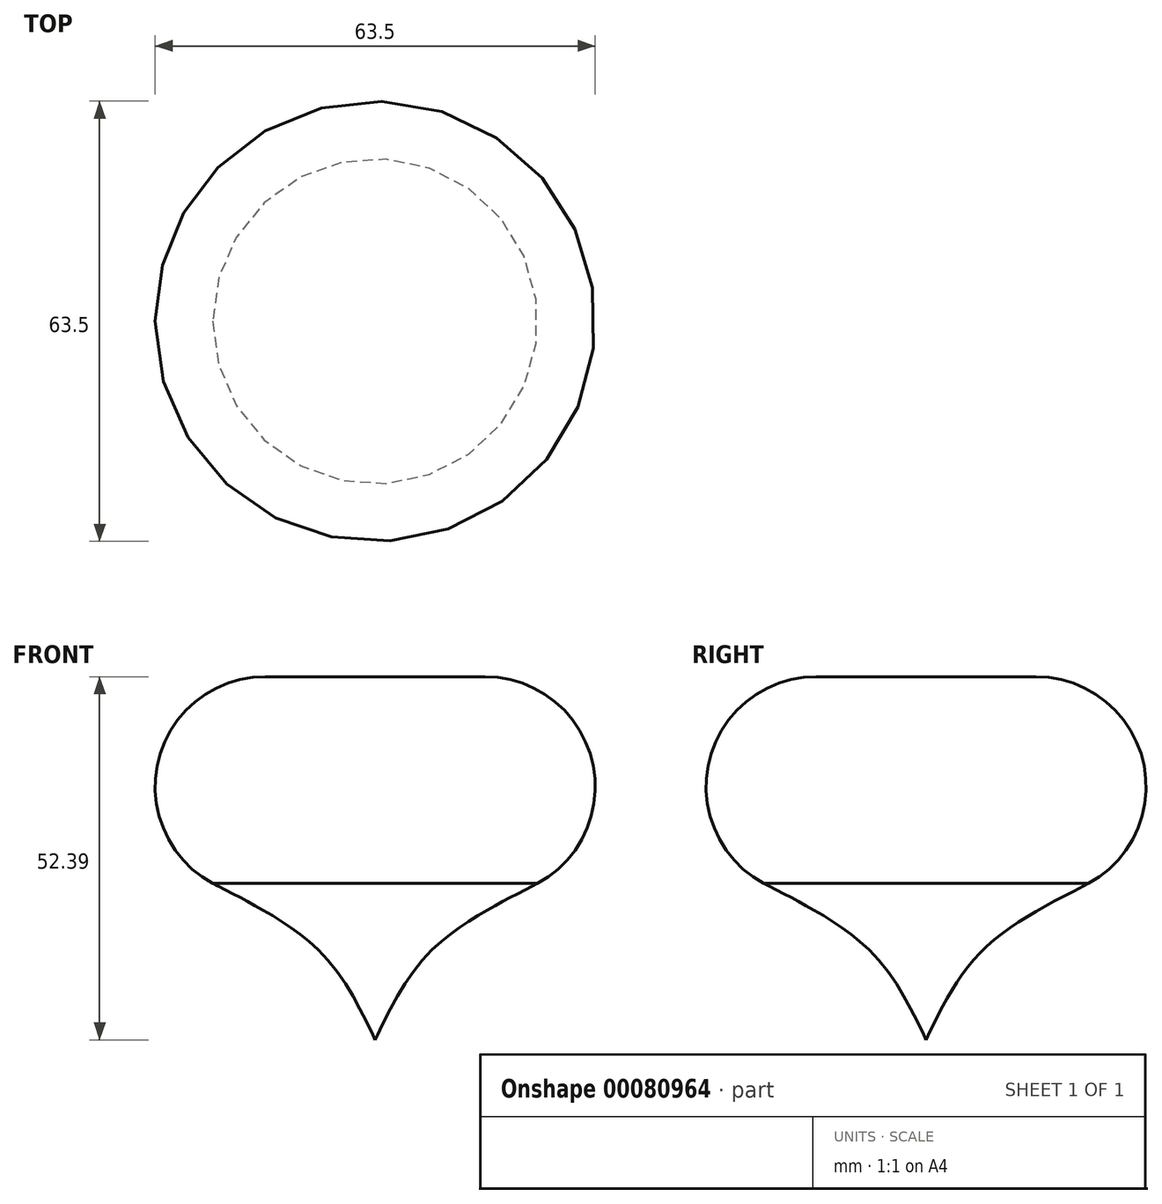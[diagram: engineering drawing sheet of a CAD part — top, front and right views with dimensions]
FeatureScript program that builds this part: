
annotation { "Feature Type Name" : "Feature", "Feature Type Description" : "" }
export const myFeature = defineFeature(function(context is Context, id is Id, definition is map)
    precondition{}
    {
        {
            var Q0;
            Q0=qCreatedBy(makeId("Right.planeOp"),FACE);
            var sketch = newSketch(context, id + "F0", { "sketchPlane" : qUnion([Q0])});
            skLineSegment(sketch, "E0", {"start": v(15.88, 31.75) * mm, "end": v(15.88, 47.62) * mm});
            skCircle(sketch, "E1", {"center": v(15.88, 47.62) * mm, "radius": 15.88 * mm});
            skLineSegment(sketch, "E2", {"start": v(0, 63.5) * mm, "end": v(15.87, 63.5) * mm});
            skFitSpline(sketch, "E3", {"points": [v(0, 11.11) * mm, v(7.94, 23.81) * mm, v(23.43, 33.66) * mm], "startDerivative": vector(13.7, 28.66) * mm, "endDerivative": vector(32.82, 16.67) * mm});
            skLineSegment(sketch, "E4", {"start": v(0, 11.11) * mm, "end": v(0, 63.5) * mm});
            skSolve(sketch);
        }
        {
            var Q0;
            {var subQ0=sQuery(id+"F0.wireOp",EDGE,"E2");Q0=makeQuery(id+"F0.imprint","IMPRINT",FACE,{"disambiguationData":[TD([[makeQuery(id+"F0.imprint","IMPRINT",EDGE,{"derivedFrom":subQ0}),-1.0]])]});}
            var Q1;
            {var subQ0=sQuery(id+"F0.wireOp",EDGE,"E1");var subQ4=makeQuery(id+"F0.imprint","IMPRINT",VERTEX,{"derivedFrom":subQ0});Q1=makeQuery(id+"F0.imprint","IMPRINT",FACE,{"disambiguationData":[TD([[makeQuery(id+"F0.imprint","IMPRINT",EDGE,{"disambiguationData":[TD([[subQ4,1.0]])],"derivedFrom":subQ0}),1.0]])]});}
            var Q2;
            {var subQ0=sQuery(id+"F0.wireOp",EDGE,"E1");var subQ1=makeQuery(id+"F0.imprint","IMPRINT",VERTEX,{"derivedFrom":subQ0});Q2=makeQuery(id+"F0.imprint","IMPRINT",FACE,{"disambiguationData":[TD([[makeQuery(id+"F0.imprint","IMPRINT",EDGE,{"disambiguationData":[TD([[subQ1,1.0]])],"derivedFrom":subQ0}),-1.0]])]});}
            var Q3;
            Q3=sQuery(id+"F0.wireOp",EDGE,"E4");
            revolve(context, id + "F1", {"entities" : qUnion([Q0, Q1, Q2]), "axis" : qUnion([Q3]), "revolveType" : RevolveType.FULL});
        }
    });
